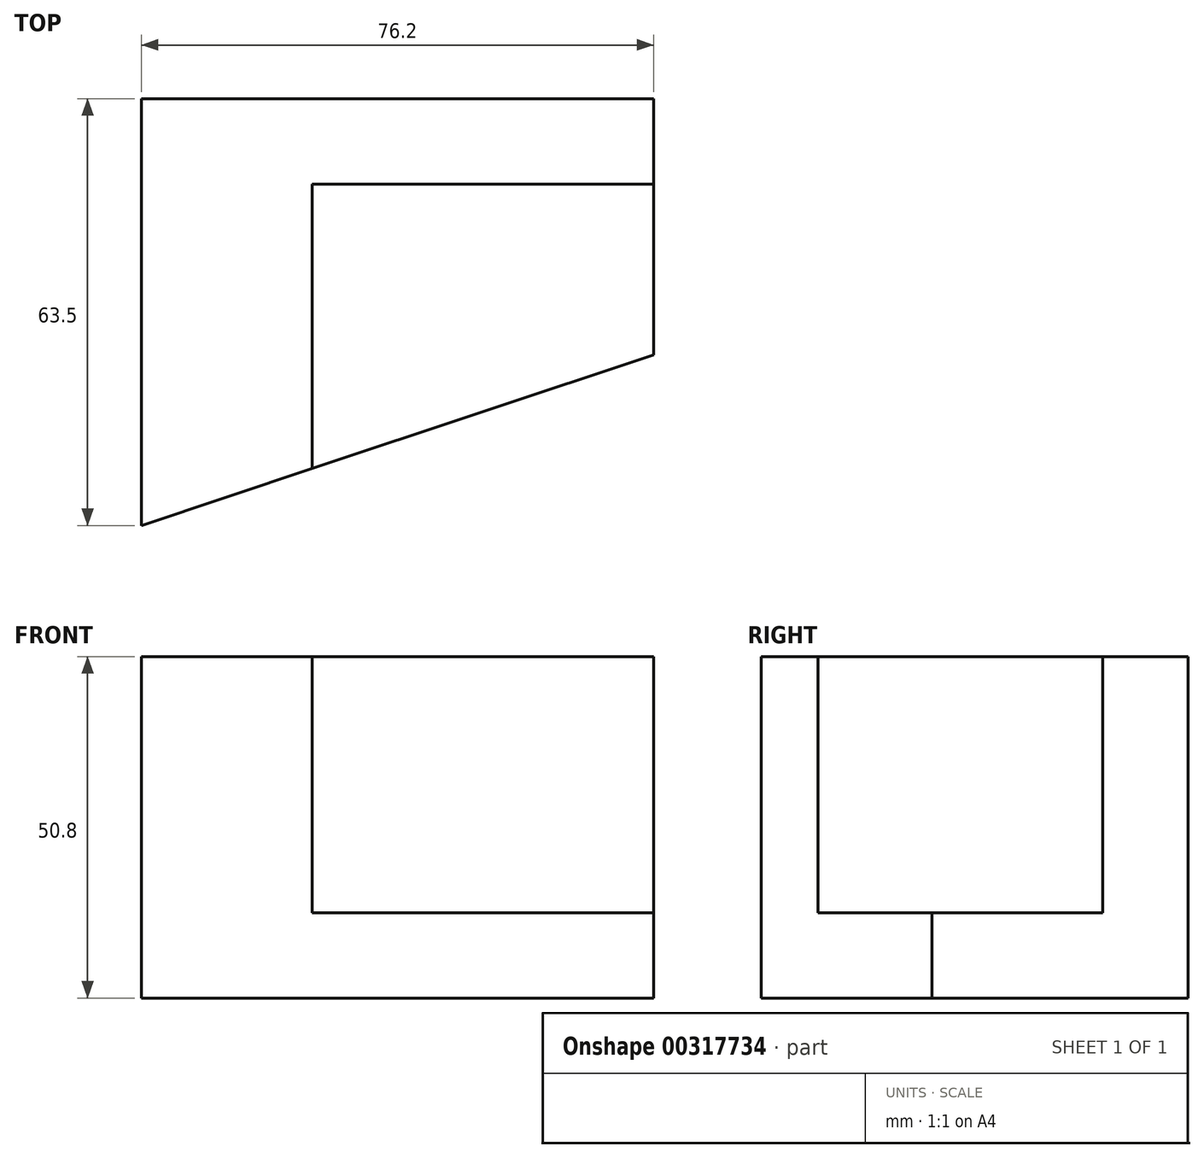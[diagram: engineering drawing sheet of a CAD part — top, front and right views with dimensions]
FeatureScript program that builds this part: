
annotation { "Feature Type Name" : "Feature", "Feature Type Description" : "" }
export const myFeature = defineFeature(function(context is Context, id is Id, definition is map)
    precondition{}
    {
        {
            var Q0;
            Q0=qCreatedBy(makeId("Front.planeOp"),FACE);
            var sketch = newSketch(context, id + "F0", { "sketchPlane" : qUnion([Q0])});
            skLineSegment(sketch, "E0.bottom", {"start": v(0, 0) * mm, "end": v(76.2, 0) * mm});
            skLineSegment(sketch, "E0.top", {"start": v(0, 50.8) * mm, "end": v(76.2, 50.8) * mm});
            skLineSegment(sketch, "E0.left", {"start": v(0, 0) * mm, "end": v(0, 50.8) * mm});
            skLineSegment(sketch, "E0.right", {"start": v(76.2, 0) * mm, "end": v(76.2, 50.8) * mm});
            skLineSegment(sketch, "E1", {"start": v(25.4, 50.8) * mm, "end": v(25.4, 12.7) * mm});
            skLineSegment(sketch, "E2", {"start": v(25.4, 12.7) * mm, "end": v(76.2, 12.7) * mm});
            skSolve(sketch);
        }
        {
            var Q0;
            {var subQ1=sQuery(id+"F0.wireOp",EDGE,"E0.bottom");Q0=makeQuery(id+"F0.imprint","IMPRINT",FACE,{"disambiguationData":[TD([[makeQuery(id+"F0.imprint","IMPRINT",EDGE,{"derivedFrom":subQ1}),1.0]])]});}
            extrude(context, id + "F1", {"entities" : qUnion([Q0]), "depth" : 63.5 * mm});
        }
        {
            var Q0;
            {var subQ3=sQuery(id+"F0.wireOp",EDGE,"E1");Q0=makeQuery(id+"F0.imprint","IMPRINT",FACE,{"disambiguationData":[TD([[makeQuery(id+"F0.imprint","IMPRINT",EDGE,{"derivedFrom":subQ3}),1.0]])]});}
            extrude(context, id + "F2", {"entities" : qUnion([Q0]), "operationType" : NewBodyOperationType.ADD, "depth" : 12.7 * mm});
        }
        {
            var Q0;
            Q0=makeQuery(id+"F1.opExtrude","SWEPT_FACE",FACE,{"disambiguationData":[OSD([sQuery(id+"F0.wireOp",EDGE,"E0.bottom")])]});
            var sketch = newSketch(context, id + "F3", { "sketchPlane" : qUnion([Q0])});
            skLineSegment(sketch, "E3", {"start": v(0, 63.5) * mm, "end": v(76.2, 38.1) * mm});
            skLineSegment(sketch, "E4", {"start": v(76.2, 38.1) * mm, "end": v(76.2, 63.5) * mm});
            skLineSegment(sketch, "E5", {"start": v(76.2, 63.5) * mm, "end": v(0, 63.5) * mm});
            skSolve(sketch);
        }
        {
            var Q0;
            Q0 = qSketchRegion(id + "F3", true);
            extrude(context, id + "F4", {"entities" : qUnion([Q0]), "operationType" : NewBodyOperationType.REMOVE, "endBound" : BoundingType.THROUGH_ALL, "oppositeDirection" : true, "depth" : 25.4 * mm});
        }
    });
